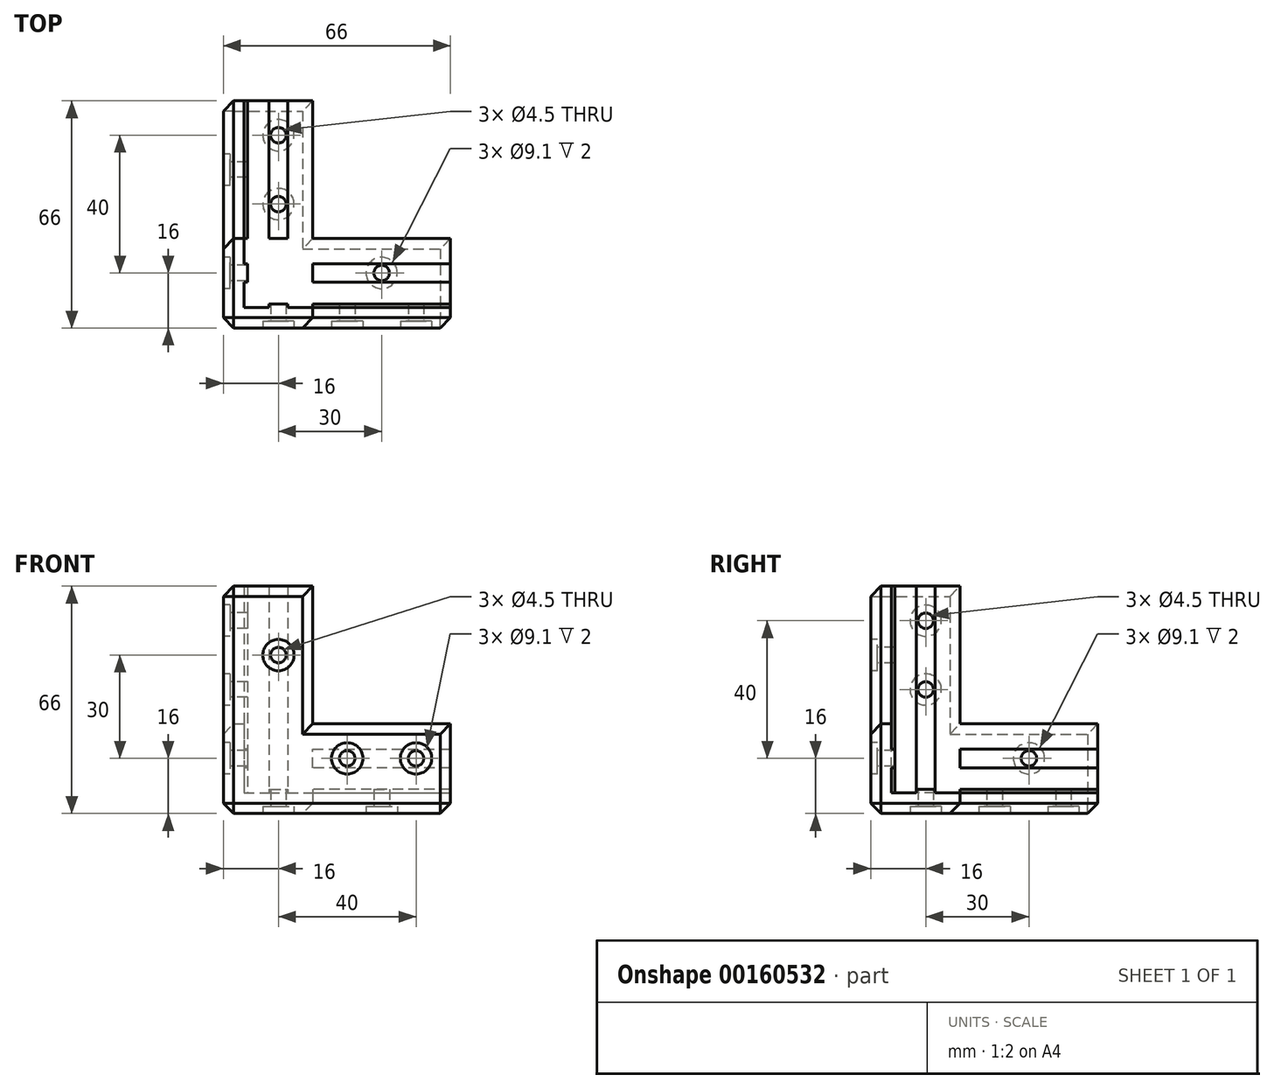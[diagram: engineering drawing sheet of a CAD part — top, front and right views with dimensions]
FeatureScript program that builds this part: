
annotation { "Feature Type Name" : "Feature", "Feature Type Description" : "" }
export const myFeature = defineFeature(function(context is Context, id is Id, definition is map)
    precondition{}
    {
        {
            var Q0;
            Q0=qCreatedBy(makeId("Top.planeOp"),FACE);
            var sketch = newSketch(context, id + "F0", { "sketchPlane" : qUnion([Q0])});
            skLineSegment(sketch, "E0", {"start": v(0, 0) * mm, "end": v(0, 66) * mm});
            skLineSegment(sketch, "E1", {"start": v(0, 66) * mm, "end": v(26, 66) * mm});
            skLineSegment(sketch, "E2", {"start": v(26, 66) * mm, "end": v(26, 26) * mm});
            skLineSegment(sketch, "E3", {"start": v(26, 26) * mm, "end": v(66, 26) * mm});
            skLineSegment(sketch, "E4", {"start": v(66, 26) * mm, "end": v(66, 0) * mm});
            skLineSegment(sketch, "E5", {"start": v(66, 0) * mm, "end": v(0, 0) * mm});
            skLineSegment(sketch, "E6", {"start": v(66, 6) * mm, "end": v(6, 6) * mm, "construction": true});
            skLineSegment(sketch, "E7", {"start": v(6, 6) * mm, "end": v(6, 66) * mm, "construction": true});
            skSolve(sketch);
        }
        {
            var Q0;
            Q0=qSketchRegion(id+"F0",true);
            extrude(context, id + "F1", {"entities" : qUnion([Q0]), "depth" : 6 * mm});
        }
        {
            var Q0;
            Q0=makeQuery(id+"F1.opExtrude","CAP_FACE",FACE,{"disambiguationData":[OSD([sQuery(id+"F0.wireOp",EDGE,"E0"),sQuery(id+"F0.wireOp",EDGE,"E1"),sQuery(id+"F0.wireOp",EDGE,"E2"),sQuery(id+"F0.wireOp",EDGE,"E3"),sQuery(id+"F0.wireOp",EDGE,"E4"),sQuery(id+"F0.wireOp",EDGE,"E5")])],"isStart":false});
            var sketch = newSketch(context, id + "F2", { "sketchPlane" : qUnion([Q0])});
            skLineSegment(sketch, "E8", {"start": v(0, 66) * mm, "end": v(6, 66) * mm});
            skLineSegment(sketch, "E9", {"start": v(6, 66) * mm, "end": v(6, 6) * mm});
            skLineSegment(sketch, "E10", {"start": v(6, 6) * mm, "end": v(66, 6) * mm});
            skLineSegment(sketch, "E11", {"start": v(66, 6) * mm, "end": v(66, 0) * mm});
            skLineSegment(sketch, "E12", {"start": v(66, 0) * mm, "end": v(0, 0) * mm});
            skLineSegment(sketch, "E13", {"start": v(0, 0) * mm, "end": v(0, 66) * mm});
            skSolve(sketch);
        }
        {
            var Q0;
            Q0=makeQuery(id+"F2.imprint","IMPRINT",FACE,{"disambiguationData":[TD([[makeQuery(id+"F2.imprint","IMPRINT",EDGE,{"derivedFrom":sQuery(id+"F2.wireOp",EDGE,"E8")}),-1.0]])]});
            extrude(context, id + "F3", {"entities" : qUnion([Q0]), "operationType" : NewBodyOperationType.ADD, "depth" : 20 * mm});
        }
        {
            var Q0;
            Q0=makeQuery(id+"F3.opExtrude","CAP_FACE",FACE,{"disambiguationData":[OSD([sQuery(id+"F2.wireOp",EDGE,"E8"),sQuery(id+"F2.wireOp",EDGE,"E9"),sQuery(id+"F2.wireOp",EDGE,"E10"),sQuery(id+"F2.wireOp",EDGE,"E11"),sQuery(id+"F2.wireOp",EDGE,"E12"),sQuery(id+"F2.wireOp",EDGE,"E13")])],"isStart":false});
            var sketch = newSketch(context, id + "F4", { "sketchPlane" : qUnion([Q0])});
            skLineSegment(sketch, "E14", {"start": v(6, 26) * mm, "end": v(0, 26) * mm});
            skLineSegment(sketch, "E15", {"start": v(0, 26) * mm, "end": v(0, 0) * mm});
            skLineSegment(sketch, "E16", {"start": v(0, 0) * mm, "end": v(26, 0) * mm});
            skLineSegment(sketch, "E17", {"start": v(26, 0) * mm, "end": v(26, 6) * mm});
            skLineSegment(sketch, "E18", {"start": v(26, 6) * mm, "end": v(6, 6) * mm});
            skLineSegment(sketch, "E19", {"start": v(6, 6) * mm, "end": v(6, 26) * mm});
            skSolve(sketch);
        }
        {
            var Q0;
            Q0=qSketchRegion(id+"F4",true);
            extrude(context, id + "F5", {"entities" : qUnion([Q0]), "operationType" : NewBodyOperationType.ADD, "depth" : 40 * mm});
        }
        {
            var Q0;
            Q0=makeQuery(id+"F1.opExtrude","CAP_FACE",FACE,{"disambiguationData":[OSD([sQuery(id+"F0.wireOp",EDGE,"E0"),sQuery(id+"F0.wireOp",EDGE,"E1"),sQuery(id+"F0.wireOp",EDGE,"E2"),sQuery(id+"F0.wireOp",EDGE,"E3"),sQuery(id+"F0.wireOp",EDGE,"E4"),sQuery(id+"F0.wireOp",EDGE,"E5")])],"isStart":false});
            var sketch = newSketch(context, id + "F6", { "sketchPlane" : qUnion([Q0])});
            skLineSegment(sketch, "E20", {"start": v(66, 16) * mm, "end": v(6, 16) * mm, "construction": true});
            skLineSegment(sketch, "E21", {"start": v(16, 66) * mm, "end": v(16, 6) * mm, "construction": true});
            skLineSegment(sketch, "E22", {"start": v(16, 6) * mm, "end": v(18.71, 6) * mm});
            skLineSegment(sketch, "E23", {"start": v(18.71, 6) * mm, "end": v(18.71, 7) * mm});
            skLineSegment(sketch, "E24", {"start": v(18.71, 7) * mm, "end": v(13.3, 7) * mm});
            skLineSegment(sketch, "E25", {"start": v(13.3, 7) * mm, "end": v(13.3, 6) * mm});
            skLineSegment(sketch, "E26", {"start": v(13.3, 6) * mm, "end": v(16, 6) * mm});
            skLineSegment(sketch, "E27", {"start": v(6, 16) * mm, "end": v(6, 18.7) * mm});
            skLineSegment(sketch, "E28", {"start": v(6, 18.7) * mm, "end": v(7, 18.7) * mm});
            skLineSegment(sketch, "E29", {"start": v(7, 18.7) * mm, "end": v(7, 13.29) * mm});
            skLineSegment(sketch, "E30", {"start": v(7, 13.29) * mm, "end": v(6, 13.29) * mm});
            skLineSegment(sketch, "E31", {"start": v(6, 13.29) * mm, "end": v(6, 16) * mm});
            skSolve(sketch);
        }
        {
            var Q0;
            Q0=qSketchRegion(id+"F6",true);
            extrude(context, id + "F7", {"entities" : qUnion([Q0]), "operationType" : NewBodyOperationType.ADD, "depth" : 60 * mm});
        }
        {
            var Q0;
            Q0=makeQuery(id+"F1.opExtrude","CAP_FACE",FACE,{"disambiguationData":[OSD([sQuery(id+"F0.wireOp",EDGE,"E0"),sQuery(id+"F0.wireOp",EDGE,"E1"),sQuery(id+"F0.wireOp",EDGE,"E2"),sQuery(id+"F0.wireOp",EDGE,"E3"),sQuery(id+"F0.wireOp",EDGE,"E4"),sQuery(id+"F0.wireOp",EDGE,"E5")])],"isStart":false});
            var sketch = newSketch(context, id + "F8", { "sketchPlane" : qUnion([Q0])});
            skLineSegment(sketch, "E32", {"start": v(66, 16) * mm, "end": v(7, 16) * mm, "construction": true});
            skLineSegment(sketch, "E33", {"start": v(66, 16) * mm, "end": v(66, 18.7) * mm});
            skLineSegment(sketch, "E34", {"start": v(66, 18.7) * mm, "end": v(26, 18.7) * mm});
            skLineSegment(sketch, "E35", {"start": v(26, 18.7) * mm, "end": v(26, 13.29) * mm});
            skLineSegment(sketch, "E36", {"start": v(26, 13.29) * mm, "end": v(66, 13.29) * mm});
            skLineSegment(sketch, "E37", {"start": v(66, 13.29) * mm, "end": v(66, 16) * mm});
            skLineSegment(sketch, "E38", {"start": v(16, 66) * mm, "end": v(16, 7) * mm, "construction": true});
            skLineSegment(sketch, "E39", {"start": v(16, 66) * mm, "end": v(13.3, 66) * mm});
            skLineSegment(sketch, "E40", {"start": v(13.3, 66) * mm, "end": v(13.3, 26) * mm});
            skLineSegment(sketch, "E41", {"start": v(13.3, 26) * mm, "end": v(18.7, 26) * mm});
            skLineSegment(sketch, "E42", {"start": v(18.7, 26) * mm, "end": v(18.7, 66) * mm});
            skLineSegment(sketch, "E43", {"start": v(18.7, 66) * mm, "end": v(16, 66) * mm});
            skSolve(sketch);
        }
        {
            var Q0;
            Q0=qSketchRegion(id+"F8",true);
            extrude(context, id + "F9", {"entities" : qUnion([Q0]), "operationType" : NewBodyOperationType.ADD, "flatOperationType" : FlatOperationType.REMOVE, "offsetDistance" : 25 * mm, "depth" : 1 * mm, "domain" : OperationDomain.MODEL});
        }
        {
            var Q0;
            {var subQ1=sQuery(id+"F2.wireOp",EDGE,"E10");var subQ2=sQuery(id+"F0.wireOp",EDGE,"E4");var subQ3=sQuery(id+"F4.wireOp",EDGE,"E18");Q0=makeQuery(id+"F7.boolean.opBoolean","SPLIT",FACE,{"disambiguationData":[TD([makeQuery(id+"F1.opExtrude","SWEPT_FACE",FACE,{"disambiguationData":[OSD([subQ2])]})])],"derivedFrom":makeQuery(id+"F5.boolean.opBoolean","MERGE",FACE,{"derivedFrom":[makeQuery(id+"F3.opExtrude","SWEPT_FACE",FACE,{"disambiguationData":[OSD([subQ1])]}),makeQuery(id+"F5.opExtrude","SWEPT_FACE",FACE,{"disambiguationData":[OSD([subQ3])]})]})});}
            var sketch = newSketch(context, id + "F10", { "sketchPlane" : qUnion([Q0])});
            skLineSegment(sketch, "E44", {"start": v(-66, 16) * mm, "end": v(-26, 16) * mm, "construction": true});
            skLineSegment(sketch, "E45", {"start": v(-66, 16) * mm, "end": v(-66, 13.3) * mm});
            skLineSegment(sketch, "E46", {"start": v(-66, 13.3) * mm, "end": v(-26, 13.3) * mm});
            skLineSegment(sketch, "E47", {"start": v(-26, 13.3) * mm, "end": v(-26, 16) * mm});
            skLineSegment(sketch, "E48", {"start": v(-26, 18.71) * mm, "end": v(-66, 18.71) * mm});
            skLineSegment(sketch, "E49", {"start": v(-66, 18.71) * mm, "end": v(-66, 16) * mm});
            skLineSegment(sketch, "E50", {"start": v(-26, 18.71) * mm, "end": v(-26, 16) * mm});
            skSolve(sketch);
        }
        {
            var Q0;
            Q0=qSketchRegion(id+"F10",true);
            extrude(context, id + "F11", {"entities" : qUnion([Q0]), "operationType" : NewBodyOperationType.ADD, "flatOperationType" : FlatOperationType.REMOVE, "offsetDistance" : 25 * mm, "depth" : 1 * mm, "domain" : OperationDomain.MODEL});
        }
        {
            var Q0;
            {var subQ0=sQuery(id+"F2.wireOp",EDGE,"E9");var subQ3=sQuery(id+"F0.wireOp",EDGE,"E1");var subQ5=sQuery(id+"F4.wireOp",EDGE,"E19");Q0=makeQuery(id+"F7.boolean.opBoolean","SPLIT",FACE,{"disambiguationData":[TD([makeQuery(id+"F1.opExtrude","SWEPT_FACE",FACE,{"disambiguationData":[OSD([subQ3])]})])],"derivedFrom":makeQuery(id+"F5.boolean.opBoolean","MERGE",FACE,{"derivedFrom":[makeQuery(id+"F3.opExtrude","SWEPT_FACE",FACE,{"disambiguationData":[OSD([subQ0])]}),makeQuery(id+"F5.opExtrude","SWEPT_FACE",FACE,{"disambiguationData":[OSD([subQ5])]})]})});}
            var sketch = newSketch(context, id + "F12", { "sketchPlane" : qUnion([Q0])});
            skLineSegment(sketch, "E51", {"start": v(66, 16) * mm, "end": v(26, 16) * mm, "construction": true});
            skLineSegment(sketch, "E52", {"start": v(66, 16) * mm, "end": v(66, 18.71) * mm});
            skLineSegment(sketch, "E53", {"start": v(66, 18.71) * mm, "end": v(26, 18.7) * mm});
            skLineSegment(sketch, "E54", {"start": v(26, 18.7) * mm, "end": v(26, 13.29) * mm});
            skLineSegment(sketch, "E55", {"start": v(26, 13.29) * mm, "end": v(66, 13.29) * mm});
            skLineSegment(sketch, "E56", {"start": v(66, 16) * mm, "end": v(66, 13.29) * mm});
            skSolve(sketch);
        }
        {
            var Q0;
            Q0=qSketchRegion(id+"F12",true);
            extrude(context, id + "F13", {"entities" : qUnion([Q0]), "operationType" : NewBodyOperationType.ADD, "flatOperationType" : FlatOperationType.REMOVE, "offsetDistance" : 25 * mm, "depth" : 1 * mm, "domain" : OperationDomain.MODEL});
        }
        {
            var Q0;
            Q0=makeQuery(id+"F5.boolean.opBoolean","MERGE",FACE,{"derivedFrom":[makeQuery(id+"F3.boolean.opBoolean","MERGE",FACE,{"derivedFrom":[makeQuery(id+"F1.opExtrude","SWEPT_FACE",FACE,{"disambiguationData":[OSD([sQuery(id+"F0.wireOp",EDGE,"E5")])]}),makeQuery(id+"F3.opExtrude","SWEPT_FACE",FACE,{"disambiguationData":[OSD([sQuery(id+"F2.wireOp",EDGE,"E12")])]})]}),makeQuery(id+"F5.opExtrude","SWEPT_FACE",FACE,{"disambiguationData":[OSD([sQuery(id+"F4.wireOp",EDGE,"E16")])]})]});
            var sketch = newSketch(context, id + "F14", { "sketchPlane" : qUnion([Q0])});
            skLineSegment(sketch, "E57", {"start": v(6, 66) * mm, "end": v(6, 6) * mm, "construction": true});
            skLineSegment(sketch, "E58", {"start": v(6, 6) * mm, "end": v(66, 6) * mm, "construction": true});
            skCircle(sketch, "E59", {"center": v(56, 16) * mm, "radius": 2.25 * mm});
            skCircle(sketch, "E60", {"center": v(36, 16) * mm, "radius": 2.25 * mm});
            skCircle(sketch, "E61", {"center": v(16, 46) * mm, "radius": 2.25 * mm});
            skLineSegment(sketch, "E62", {"start": v(26, 26) * mm, "end": v(6, 26) * mm, "construction": true});
            skLineSegment(sketch, "E63", {"start": v(26, 26) * mm, "end": v(26, 6) * mm, "construction": true});
            skSolve(sketch);
        }
        {
            var Q0;
            Q0=makeQuery(id+"F14.imprint","IMPRINT",FACE,{"disambiguationData":[TD([[makeQuery(id+"F14.imprint","IMPRINT",EDGE,{"derivedFrom":sQuery(id+"F14.wireOp",EDGE,"E59")}),1.0]])]});
            var Q1;
            Q1=makeQuery(id+"F14.imprint","IMPRINT",FACE,{"disambiguationData":[TD([[makeQuery(id+"F14.imprint","IMPRINT",EDGE,{"derivedFrom":sQuery(id+"F14.wireOp",EDGE,"E61")}),1.0]])]});
            var Q2;
            Q2=makeQuery(id+"F14.imprint","IMPRINT",FACE,{"disambiguationData":[TD([[makeQuery(id+"F14.imprint","IMPRINT",EDGE,{"derivedFrom":sQuery(id+"F14.wireOp",EDGE,"E60")}),1.0]])]});
            extrude(context, id + "F15", {"entities" : qUnion([Q0, Q1, Q2]), "operationType" : NewBodyOperationType.REMOVE, "endBound" : BoundingType.UP_TO_NEXT, "oppositeDirection" : true, "depth" : 25 * mm});
        }
        {
            var Q0;
            Q0=makeQuery(id+"F5.boolean.opBoolean","MERGE",FACE,{"derivedFrom":[makeQuery(id+"F3.boolean.opBoolean","MERGE",FACE,{"derivedFrom":[makeQuery(id+"F1.opExtrude","SWEPT_FACE",FACE,{"disambiguationData":[OSD([sQuery(id+"F0.wireOp",EDGE,"E0")])]}),makeQuery(id+"F3.opExtrude","SWEPT_FACE",FACE,{"disambiguationData":[OSD([sQuery(id+"F2.wireOp",EDGE,"E13")])]})]}),makeQuery(id+"F5.opExtrude","SWEPT_FACE",FACE,{"disambiguationData":[OSD([sQuery(id+"F4.wireOp",EDGE,"E15")])]})]});
            var sketch = newSketch(context, id + "F16", { "sketchPlane" : qUnion([Q0])});
            skLineSegment(sketch, "E64", {"start": v(-6, 66) * mm, "end": v(-6, 6) * mm, "construction": true});
            skLineSegment(sketch, "E65", {"start": v(-6, 6) * mm, "end": v(-66, 6) * mm, "construction": true});
            skCircle(sketch, "E66", {"center": v(-16, 56) * mm, "radius": 2.25 * mm});
            skCircle(sketch, "E67", {"center": v(-46, 16) * mm, "radius": 2.25 * mm});
            skCircle(sketch, "E68", {"center": v(-16, 36) * mm, "radius": 2.25 * mm});
            skSolve(sketch);
        }
        {
            var Q0;
            Q0=qSketchRegion(id+"F16",true);
            extrude(context, id + "F17", {"entities" : qUnion([Q0]), "operationType" : NewBodyOperationType.REMOVE, "endBound" : BoundingType.UP_TO_NEXT, "oppositeDirection" : true, "depth" : 25 * mm});
        }
        {
            var Q0;
            Q0=makeQuery(id+"F1.opExtrude","CAP_FACE",FACE,{"disambiguationData":[OSD([sQuery(id+"F0.wireOp",EDGE,"E0"),sQuery(id+"F0.wireOp",EDGE,"E1"),sQuery(id+"F0.wireOp",EDGE,"E2"),sQuery(id+"F0.wireOp",EDGE,"E3"),sQuery(id+"F0.wireOp",EDGE,"E4"),sQuery(id+"F0.wireOp",EDGE,"E5")])],"isStart":true});
            var sketch = newSketch(context, id + "F18", { "sketchPlane" : qUnion([Q0])});
            skLineSegment(sketch, "E69", {"start": v(66, -6) * mm, "end": v(6, -6) * mm, "construction": true});
            skLineSegment(sketch, "E70", {"start": v(6, -6) * mm, "end": v(6, -66) * mm, "construction": true});
            skCircle(sketch, "E71", {"center": v(46, -16) * mm, "radius": 2.25 * mm});
            skCircle(sketch, "E72", {"center": v(16, -56) * mm, "radius": 2.25 * mm});
            skCircle(sketch, "E73", {"center": v(16, -36) * mm, "radius": 2.25 * mm});
            skSolve(sketch);
        }
        {
            var Q0;
            Q0=qSketchRegion(id+"F18",true);
            extrude(context, id + "F19", {"entities" : qUnion([Q0]), "operationType" : NewBodyOperationType.REMOVE, "endBound" : BoundingType.UP_TO_NEXT, "oppositeDirection" : true, "depth" : 25 * mm});
        }
        {
            var Q0;
            Q0=makeQuery(id+"F5.boolean.opBoolean","MERGE",FACE,{"derivedFrom":[makeQuery(id+"F3.boolean.opBoolean","MERGE",FACE,{"derivedFrom":[makeQuery(id+"F1.opExtrude","SWEPT_FACE",FACE,{"disambiguationData":[OSD([sQuery(id+"F0.wireOp",EDGE,"E5")])]}),makeQuery(id+"F3.opExtrude","SWEPT_FACE",FACE,{"disambiguationData":[OSD([sQuery(id+"F2.wireOp",EDGE,"E12")])]})]}),makeQuery(id+"F5.opExtrude","SWEPT_FACE",FACE,{"disambiguationData":[OSD([sQuery(id+"F4.wireOp",EDGE,"E16")])]})]});
            var sketch = newSketch(context, id + "F20", { "sketchPlane" : qUnion([Q0])});
            skCircle(sketch, "E74", {"center": v(16, 46) * mm, "radius": 4.55 * mm});
            skCircle(sketch, "E75", {"center": v(36, 16) * mm, "radius": 4.55 * mm});
            skCircle(sketch, "E76", {"center": v(56, 16) * mm, "radius": 4.55 * mm});
            skSolve(sketch);
        }
        {
            var Q0;
            Q0=qSketchRegion(id+"F20",true);
            extrude(context, id + "F21", {"entities" : qUnion([Q0]), "operationType" : NewBodyOperationType.REMOVE, "oppositeDirection" : true, "depth" : 2 * mm});
        }
        {
            var Q0;
            Q0=makeQuery(id+"F5.boolean.opBoolean","MERGE",FACE,{"derivedFrom":[makeQuery(id+"F3.boolean.opBoolean","MERGE",FACE,{"derivedFrom":[makeQuery(id+"F1.opExtrude","SWEPT_FACE",FACE,{"disambiguationData":[OSD([sQuery(id+"F0.wireOp",EDGE,"E0")])]}),makeQuery(id+"F3.opExtrude","SWEPT_FACE",FACE,{"disambiguationData":[OSD([sQuery(id+"F2.wireOp",EDGE,"E13")])]})]}),makeQuery(id+"F5.opExtrude","SWEPT_FACE",FACE,{"disambiguationData":[OSD([sQuery(id+"F4.wireOp",EDGE,"E15")])]})]});
            var sketch = newSketch(context, id + "F22", { "sketchPlane" : qUnion([Q0])});
            skCircle(sketch, "E77", {"center": v(-16, 56) * mm, "radius": 4.55 * mm});
            skCircle(sketch, "E78", {"center": v(-46, 16) * mm, "radius": 4.55 * mm});
            skCircle(sketch, "E79", {"center": v(-16, 36) * mm, "radius": 4.55 * mm});
            skSolve(sketch);
        }
        {
            var Q0;
            Q0=qSketchRegion(id+"F22",true);
            extrude(context, id + "F23", {"entities" : qUnion([Q0]), "operationType" : NewBodyOperationType.REMOVE, "oppositeDirection" : true, "depth" : 2 * mm});
        }
        {
            var Q0;
            Q0=makeQuery(id+"F1.opExtrude","CAP_FACE",FACE,{"disambiguationData":[OSD([sQuery(id+"F0.wireOp",EDGE,"E0"),sQuery(id+"F0.wireOp",EDGE,"E1"),sQuery(id+"F0.wireOp",EDGE,"E2"),sQuery(id+"F0.wireOp",EDGE,"E3"),sQuery(id+"F0.wireOp",EDGE,"E4"),sQuery(id+"F0.wireOp",EDGE,"E5")])],"isStart":true});
            var sketch = newSketch(context, id + "F24", { "sketchPlane" : qUnion([Q0])});
            skCircle(sketch, "E80", {"center": v(16, -56) * mm, "radius": 4.55 * mm});
            skCircle(sketch, "E81", {"center": v(46, -16) * mm, "radius": 4.55 * mm});
            skCircle(sketch, "E82", {"center": v(16, -36) * mm, "radius": 4.55 * mm});
            skSolve(sketch);
        }
        {
            var Q0;
            Q0=qSketchRegion(id+"F24",true);
            extrude(context, id + "F25", {"entities" : qUnion([Q0]), "operationType" : NewBodyOperationType.REMOVE, "oppositeDirection" : true, "depth" : 2 * mm});
        }
        {
            var Q0;
            Q0=makeQuery(id+"F1.opExtrude","CAP_EDGE",EDGE,{"disambiguationData":[OSD([sQuery(id+"F0.wireOp",EDGE,"E5")])],"isStart":true});
            var Q1;
            Q1=makeQuery(id+"F1.opExtrude","CAP_EDGE",EDGE,{"disambiguationData":[OSD([sQuery(id+"F0.wireOp",EDGE,"E0")])],"isStart":true});
            var Q2;
            Q2=makeQuery(id+"F5.boolean.opBoolean","MERGE",EDGE,{"derivedFrom":[makeQuery(id+"F3.boolean.opBoolean","MERGE",EDGE,{"derivedFrom":[makeQuery(id+"F1.opExtrude","SWEPT_EDGE",EDGE,{"disambiguationData":[OSD([sQuery(id+"F0.wireOp",EDGE,"E0"),sQuery(id+"F0.wireOp",EDGE,"E5")])]}),makeQuery(id+"F3.opExtrude","SWEPT_EDGE",EDGE,{"disambiguationData":[OSD([sQuery(id+"F2.wireOp",EDGE,"E12"),sQuery(id+"F2.wireOp",EDGE,"E13")])]})]}),makeQuery(id+"F5.opExtrude","SWEPT_EDGE",EDGE,{"disambiguationData":[OSD([sQuery(id+"F4.wireOp",EDGE,"E15"),sQuery(id+"F4.wireOp",EDGE,"E16")])]})]});
            var Q3;
            Q3=makeQuery(id+"F5.opExtrude","SWEPT_EDGE",EDGE,{"disambiguationData":[OSD([sQuery(id+"F2.wireOp",EDGE,"E13"),sQuery(id+"F4.wireOp",EDGE,"E14"),sQuery(id+"F4.wireOp",EDGE,"E15")])]});
            var Q4;
            Q4=makeQuery(id+"F3.opExtrude","CAP_EDGE",EDGE,{"disambiguationData":[OSD([sQuery(id+"F2.wireOp",EDGE,"E13")])],"isStart":false});
            var Q5;
            Q5=makeQuery(id+"F5.opExtrude","SWEPT_EDGE",EDGE,{"disambiguationData":[OSD([sQuery(id+"F2.wireOp",EDGE,"E12"),sQuery(id+"F4.wireOp",EDGE,"E16"),sQuery(id+"F4.wireOp",EDGE,"E17")])]});
            var Q6;
            Q6=makeQuery(id+"F3.opExtrude","CAP_EDGE",EDGE,{"disambiguationData":[OSD([sQuery(id+"F2.wireOp",EDGE,"E12")])],"isStart":false});
            var Q7;
            Q7=makeQuery(id+"F5.opExtrude","CAP_EDGE",EDGE,{"disambiguationData":[OSD([sQuery(id+"F4.wireOp",EDGE,"E15")])],"isStart":false});
            var Q8;
            Q8=makeQuery(id+"F5.opExtrude","CAP_EDGE",EDGE,{"disambiguationData":[OSD([sQuery(id+"F4.wireOp",EDGE,"E16")])],"isStart":false});
            var Q9;
            Q9=makeQuery(id+"F3.boolean.opBoolean","MERGE",EDGE,{"derivedFrom":[makeQuery(id+"F1.opExtrude","SWEPT_EDGE",EDGE,{"disambiguationData":[OSD([sQuery(id+"F0.wireOp",EDGE,"E0"),sQuery(id+"F0.wireOp",EDGE,"E1")])]}),makeQuery(id+"F3.opExtrude","SWEPT_EDGE",EDGE,{"disambiguationData":[OSD([sQuery(id+"F2.wireOp",EDGE,"E8"),sQuery(id+"F2.wireOp",EDGE,"E13")])]})]});
            var Q10;
            Q10=makeQuery(id+"F1.opExtrude","CAP_EDGE",EDGE,{"disambiguationData":[OSD([sQuery(id+"F0.wireOp",EDGE,"E1")])],"isStart":true});
            var Q11;
            Q11=makeQuery(id+"F3.boolean.opBoolean","MERGE",EDGE,{"derivedFrom":[makeQuery(id+"F1.opExtrude","SWEPT_EDGE",EDGE,{"disambiguationData":[OSD([sQuery(id+"F0.wireOp",EDGE,"E4"),sQuery(id+"F0.wireOp",EDGE,"E5")])]}),makeQuery(id+"F3.opExtrude","SWEPT_EDGE",EDGE,{"disambiguationData":[OSD([sQuery(id+"F2.wireOp",EDGE,"E11"),sQuery(id+"F2.wireOp",EDGE,"E12")])]})]});
            var Q12;
            Q12=makeQuery(id+"F1.opExtrude","CAP_EDGE",EDGE,{"disambiguationData":[OSD([sQuery(id+"F0.wireOp",EDGE,"E4")])],"isStart":true});
            var Q13;
            Q13=makeQuery(id+"F1.opExtrude","CAP_EDGE",EDGE,{"disambiguationData":[OSD([sQuery(id+"F0.wireOp",EDGE,"E3")])],"isStart":true});
            var Q14;
            Q14=makeQuery(id+"F1.opExtrude","CAP_EDGE",EDGE,{"disambiguationData":[OSD([sQuery(id+"F0.wireOp",EDGE,"E2")])],"isStart":true});
            chamfer(context, id + "F26", {"entities" : qUnion([Q0, Q1, Q2, Q3, Q4, Q5, Q6, Q7, Q8, Q9, Q10, Q11, Q12, Q13, Q14]), "width" : 3 * mm, "tangentPropagation" : true});
        }
    });
